# Revit family: ir_quattro_slim_xs_058500
name_source: partatom
category: Elektroinstallationen
revit_build: Autodesk Revit 2016 (Build: 20190508_0715(x64)
units: mm (PartAtom-declared; Revit-internal decimal feet)

## family parameters
Basisbauteil = Fläche
Beim Laden mit Abzugskörper schneiden = Nein
Bemaßung runder Anschluss = Durchmesser verwenden
Beschriftungsausrichtung beibehalten = Nein
Gemeinsam genutzt = Nein
Raumberechnungspunkt = Nein
Teiletyp = Normal

## types (1)
- IR Quattro SLIM XS
    Apparent Load = 0 VA
    Beschreibung = Type: Presence detector; Dimensions (L x W x H): 60 x 77 x 77 mm; Power supply, detail: KNX bus; Sensor Technology: passive infrared; Application, place: Indoors; Application, room: one-person office, hotel room, care room, function room / ancillary room, WC / washroom, Indoors; Installation site: ceiling; Installation: Concealed wiring; Electronic scalability: No; Mechanical scalability: No; Mounting height: 2,50 – 4,00 m; Optimum mounting height: 2,8 m; Detection angle: 360 °; Angle of aperture: 160 °; Sneak-by guard: Yes; Capability of masking out individual segments: No; Reach, detail: Retina lens and hexagonal Fresnel structure; Reach, radial: 4 x 4 m (16 m²); Reach, tangential: 4 x 4 m (16 m²); Reach, presence: 4 x 4 m (16 m²); Twilight setting TEACH: Yes; Twilight setting: 10 – 1000 lx; Time setting: 0 sec – 1092 min; Basic light level function: Yes; Basic light level function in per cent: 10 – 50 %; Basic light level function time: Permanently ON, 1-255 min, all night; Basic light level function percentage, from: 10 %; Basic light level function percentage, up to: 50 %; KNX functions: Photo-cell controller, Basic light level function, Light level, HVAC output, Constant-lighting control, Light output 4x, Presence output, Day / night function; With bus coupling: Yes; Settings via: ETS software, Remote control, Bus, Smart Remote; Interconnection: Yes; Type of interconnection: Master/slave, Master/master; IP-rating: IP20; Material: Plastic; Ambient temperature: 0 – 40 °C; Colour: white; Colour, RAL: 9010; Manufacturer's Warranty: 5 years; Version: KNX - square; PU1, EAN: 4007841058500
    Height = 0 mm  [stored 0 ft]
    Hersteller = Steinel
    Length = 60 mm  [stored 0.19685 ft]
    Maximum range = 2.654 m
    ModVariant = Nein
    Modell = 058500
    Mounting Place = Ceiling
    Mounting Type = Recessed
    Number of Poles = 1
    OnlyDefault = Ja
    Power Factor = 1
    Product Name = IR Quattro SLIM XS
    Product group = Presence detector
    ProductGroupID = 4
    Protection Class = Protection class
    Protection Degree = IP 20
    RlxData = <blob elided: 160189 chars, md5=3ef303f2>
    Sensor characteristics = Circular 300°-360°
    Sensor type = Passive (infrared)
    SensorDataFile = <blob elided: 166498 chars, md5=02ce23fe>
    Type of entry = Presence, Motion
    Typenbild = produkt1_058500.jpg
    Typenkommentare = Product without accessories
    URL = http://relux.com
    VarID = ---
    Voltage = 0 V
    Vorgabe-Ansicht = 1800 mm
    Weight = 0.00 kg
    Width = 77 mm

note: [stored X ft] marks values corroborated as IEEE doubles in the binary element streams (Revit-internal decimal feet)

## geometry (parser evidence)
native form markers: Sweep x20
no freeform markers — native parametric forms only
